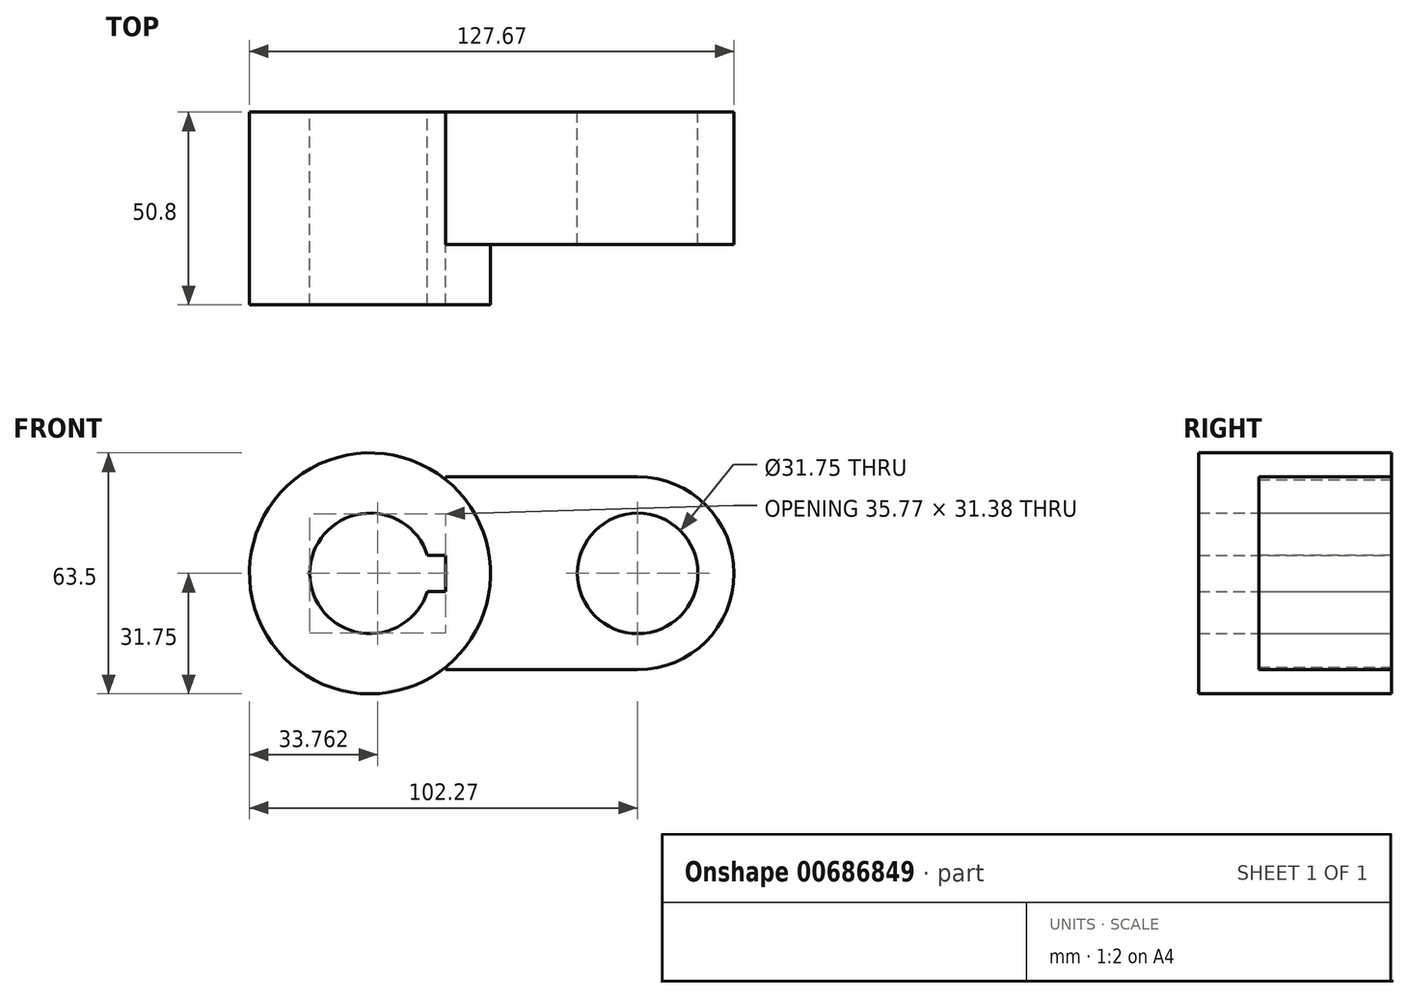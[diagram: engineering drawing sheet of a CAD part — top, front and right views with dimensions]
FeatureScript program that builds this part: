
annotation { "Feature Type Name" : "Feature", "Feature Type Description" : "" }
export const myFeature = defineFeature(function(context is Context, id is Id, definition is map)
    precondition{}
    {
        {
            var Q0;
            Q0=qCreatedBy(makeId("Front.planeOp"),FACE);
            var sketch = newSketch(context, id + "F0", { "sketchPlane" : qUnion([Q0])});
            skLineSegment(sketch, "E0.bottom", {"start": v(-9.55, 25.4) * mm, "end": v(38.1, 25.4) * mm});
            skLineSegment(sketch, "E0.top", {"start": v(-9.55, -25.4) * mm, "end": v(38.1, -25.4) * mm});
            skLineSegment(sketch, "E0.right", {"start": v(38.1, 25.4) * mm, "end": v(38.1, -25.4) * mm});
            skPoint(sketch, "E0.middle", {"position": v(0, 0) * mm});
            skCircle(sketch, "E1", {"center": v(38.1, 0) * mm, "radius": 25.4 * mm});
            skCircle(sketch, "E2", {"center": v(38.1, 0) * mm, "radius": 15.88 * mm});
            skCircle(sketch, "E3", {"center": v(38.1, 0) * mm, "radius": 9.53 * mm});
            skPoint(sketch, "E4.orphan", {"position": v(-38.1, 25.4) * mm});
            skPoint(sketch, "E5.orphan", {"position": v(-38.1, -25.4) * mm});
            skLineSegment(sketch, "E6", {"start": v(-9.55, 25.4) * mm, "end": v(-12.52, 25.4) * mm});
            skLineSegment(sketch, "E7", {"start": v(-12.52, 25.4) * mm, "end": v(-12.52, -25.4) * mm});
            skLineSegment(sketch, "E8", {"start": v(-12.52, -25.4) * mm, "end": v(-9.55, -25.4) * mm});
            skSolve(sketch);
        }
        {
            var Q0;
            Q0 = qSketchRegion(id + "F0", true);
            extrude(context, id + "F1", {"entities" : qUnion([Q0]), "depth" : 34.92 * mm, "offsetDistance" : 25.4 * mm});
        }
        {
            var Q0;
            Q0=qCreatedBy(makeId("Front.planeOp"),FACE);
            var sketch = newSketch(context, id + "F2", { "sketchPlane" : qUnion([Q0])});
            skCircle(sketch, "E9", {"center": v(-32.42, 0) * mm, "radius": 31.75 * mm});
            skArc(sketch, "E10", {"start": v(-17.27, 4.76) * mm, "mid": v(-48.3, 0) * mm, "end": v(-17.27, -4.76) * mm});
            skLineSegment(sketch, "E11", {"start": v(-17.27, 4.76) * mm, "end": v(-12.51, 4.76) * mm});
            skLineSegment(sketch, "E12", {"start": v(-12.51, -4.76) * mm, "end": v(-12.51, 4.76) * mm});
            skLineSegment(sketch, "E13", {"start": v(-12.51, -4.76) * mm, "end": v(-17.27, -4.76) * mm});
            skSolve(sketch);
        }
        {
            var Q0;
            Q0 = qSketchRegion(id + "F2", true);
            extrude(context, id + "F3", {"entities" : qUnion([Q0]), "operationType" : NewBodyOperationType.ADD, "depth" : 50.8 * mm, "offsetDistance" : 25.4 * mm});
        }
    });
